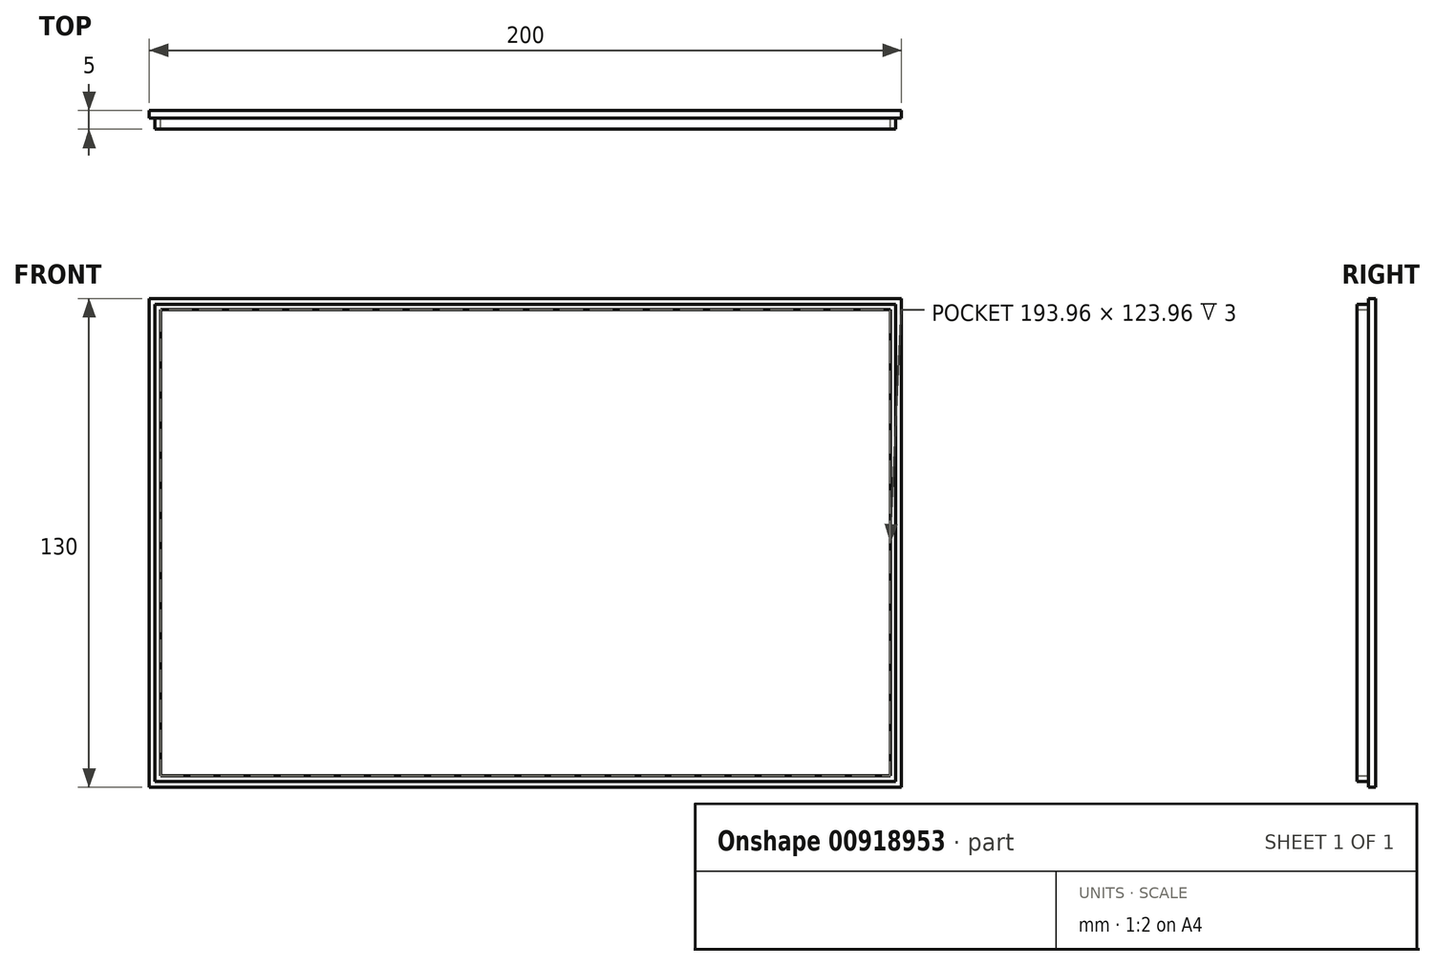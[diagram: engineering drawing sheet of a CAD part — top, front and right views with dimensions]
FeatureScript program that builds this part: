
annotation { "Feature Type Name" : "Feature", "Feature Type Description" : "" }
export const myFeature = defineFeature(function(context is Context, id is Id, definition is map)
    precondition{}
    {
        {
            var Q0;
            Q0=qCreatedBy(makeId("Front.planeOp"),FACE);
            var sketch = newSketch(context, id + "F0", { "sketchPlane" : qUnion([Q0])});
            skLineSegment(sketch, "E0.bottom", {"start": v(-52.97, 41.65) * mm, "end": v(147.03, 41.65) * mm});
            skLineSegment(sketch, "E0.top", {"start": v(-52.97, -88.35) * mm, "end": v(147.03, -88.35) * mm});
            skLineSegment(sketch, "E0.left", {"start": v(-52.97, 41.65) * mm, "end": v(-52.97, -88.35) * mm});
            skLineSegment(sketch, "E0.right", {"start": v(147.03, 41.65) * mm, "end": v(147.03, -88.35) * mm});
            skLineSegment(sketch, "E1.bottom", {"start": v(-51.45, 40.13) * mm, "end": v(145.51, 40.13) * mm});
            skLineSegment(sketch, "E1.top", {"start": v(-51.45, -86.83) * mm, "end": v(145.51, -86.83) * mm});
            skLineSegment(sketch, "E1.left", {"start": v(-51.45, 40.13) * mm, "end": v(-51.45, -86.83) * mm});
            skLineSegment(sketch, "E1.right", {"start": v(145.51, 40.13) * mm, "end": v(145.51, -86.83) * mm});
            skLineSegment(sketch, "E2.bottom", {"start": v(-49.95, 38.63) * mm, "end": v(144.01, 38.63) * mm});
            skLineSegment(sketch, "E2.top", {"start": v(-49.95, -85.33) * mm, "end": v(144.01, -85.33) * mm});
            skLineSegment(sketch, "E2.left", {"start": v(-49.95, 38.63) * mm, "end": v(-49.95, -85.33) * mm});
            skLineSegment(sketch, "E2.right", {"start": v(144.01, 38.63) * mm, "end": v(144.01, -85.33) * mm});
            skSolve(sketch);
        }
        {
            var Q0;
            Q0=makeQuery(id+"F0.imprint","IMPRINT",FACE,{"disambiguationData":[TD([[makeQuery(id+"F0.imprint","IMPRINT",EDGE,{"derivedFrom":sQuery(id+"F0.wireOp",EDGE,"E1.bottom")}),-1.0]])]});
            extrude(context, id + "F1", {"entities" : qUnion([Q0]), "depth" : 5 * mm, "offsetDistance" : 25 * mm});
        }
        {
            var Q0;
            Q0 = qSketchRegion(id + "F0", true);
            var Q1;
            Q1=makeQuery(id+"F0.imprint","IMPRINT",FACE,{"disambiguationData":[TD([[makeQuery(id+"F0.imprint","IMPRINT",EDGE,{"derivedFrom":sQuery(id+"F0.wireOp",EDGE,"E2.bottom")}),-1.0]])]});
            extrude(context, id + "F2", {"entities" : qUnion([Q0, Q1]), "operationType" : NewBodyOperationType.ADD, "depth" : 2 * mm, "offsetDistance" : 25 * mm});
        }
    });
